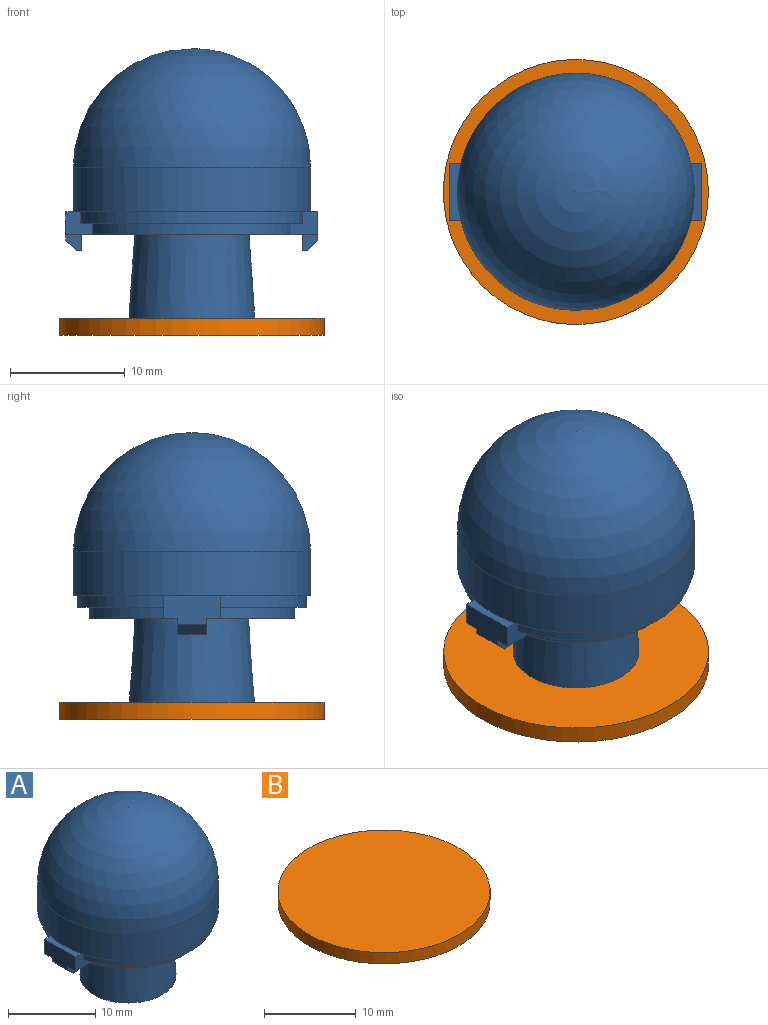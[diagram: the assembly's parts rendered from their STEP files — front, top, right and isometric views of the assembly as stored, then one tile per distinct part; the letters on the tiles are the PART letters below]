
ASSEMBLY  parts=2 mates=1
PART A: 31 faces, bbox 22x20.7x23.6 mm
  f0: plane 22x18mm, normal (0,0,-1), area 190.6mm2, adj f2,f4,f5,f6,f7,f8,f9,f10
  f1: plane 5x0.96mm, normal (0,0,1), area 3.8mm2, adj f6,f7,f8,f19
  f2: cone r=5.5mm half-angle=4deg, axis (0,0,-1), area 241.2mm2, adj f0,f3
  f3: plane 11x11mm, normal (0,0,-1), area 95mm2, adj f2
  f4: plane 2.35x2mm, normal (0,1,0), area 3.7mm2, adj f0,f5,f11,f12,f14,f15,f18
  f5: cylinder r=9mm len=17.29mm, axis (0,0,-1), area 23.2mm2, adj f0,f4,f6,f12
  f6: plane 2.35x2mm, normal (0,1,0), area 3.7mm2, adj f0,f1,f5,f7,f12,f14,f18
  f7: plane 5x2.48mm, normal (-1,0,0), area 11.2mm2, adj f0,f1,f6,f8,f24,f25,f29
  f8: plane 2.35x2mm, normal (0,-1,0), area 3.7mm2, adj f0,f1,f7,f9,f13,f16,f17
  f9: cylinder r=9mm len=17.29mm, axis (0,0,-1), area 23.2mm2, adj f0,f8,f10,f16
  f10: plane 2.35x2mm, normal (0,-1,0), area 3.7mm2, adj f0,f9,f11,f13,f15,f16,f17
  f11: plane 5x2.48mm, normal (1,0,0), area 11.2mm2, adj f0,f4,f10,f15,f21,f22,f30
  f12: plane 19.37x7.5mm, normal (0,0,-1), area 24.8mm2, adj f4,f5,f6,f14
  f13: cylinder r=10mm len=19.37mm, axis (0,0,-1), area 26.4mm2, adj f8,f10,f16,f17
  f14: cylinder r=10mm len=19.37mm, axis (0,0,-1), area 26.4mm2, adj f4,f6,f12,f18
  f15: plane 5x0.96mm, normal (0,0,1), area 3.8mm2, adj f4,f10,f11,f19
  f16: plane 19.37x7.5mm, normal (0,0,-1), area 24.8mm2, adj f8,f9,f10,f13
  f17: plane 20.09x7.85mm, normal (0,0,-1), area 9.4mm2, adj f8,f10,f13,f19
  f18: plane 20.09x7.85mm, normal (0,0,-1), area 9.4mm2, adj f4,f6,f14,f19
  f19: cylinder r=10.35mm len=20.7mm, axis (0,0,-1), area 253.6mm2, adj f1,f15,f17,f18,f28
  f20: plane 2.5x1.38mm, normal (-1,0,0), area 3.4mm2, adj f0,f21,f22,f23
  f21: plane 1.38x1.38mm, normal (0,1,0), area 1.5mm2, adj f0,f11,f20,f23,f30
  f22: plane 1.38x1.38mm, normal (0,-1,0), area 1.5mm2, adj f0,f11,f20,f23,f30
  f23: plane 2.5x0.48mm, normal (0,0,-1), area 1.2mm2, adj f20,f21,f22,f30
  f24: plane 1.38x1.38mm, normal (0,-1,0), area 1.5mm2, adj f0,f7,f26,f27,f29
  f25: plane 1.38x1.38mm, normal (0,1,0), area 1.5mm2, adj f0,f7,f26,f27,f29
  f26: plane 2.5x1.38mm, normal (1,0,0), area 3.4mm2, adj f0,f24,f25,f27
  f27: plane 2.5x0.48mm, normal (0,0,-1), area 1.2mm2, adj f24,f25,f26,f29
  f28: sphere r=10.35mm, area 673.1mm2, adj f19
  f29: plane 2.5x0.9mm, normal (-0.71,0,-0.71), area 3.2mm2, adj f7,f24,f25,f27
  f30: plane 2.5x0.9mm, normal (0.71,0,-0.71), area 3.2mm2, adj f11,f21,f22,f23
PART B: 3 faces, bbox 23.1x23.1x1.5 mm
  f0: cylinder r=11.57mm len=23.13mm, axis (0,0,-1), area 109mm2, adj f1,f2
  f1: plane 23.13x23.13mm, normal (0,0,1), area 420.3mm2, adj f0
  f2: plane 23.13x23.13mm, normal (0,0,-1), area 420.3mm2, adj f0
PLACE A t=(0,0,1.5)mm
PLACE B at identity
MATE fastened A.f2 <-> B.f0  axis (0,0,-1) through (0,0,1.5)mm
